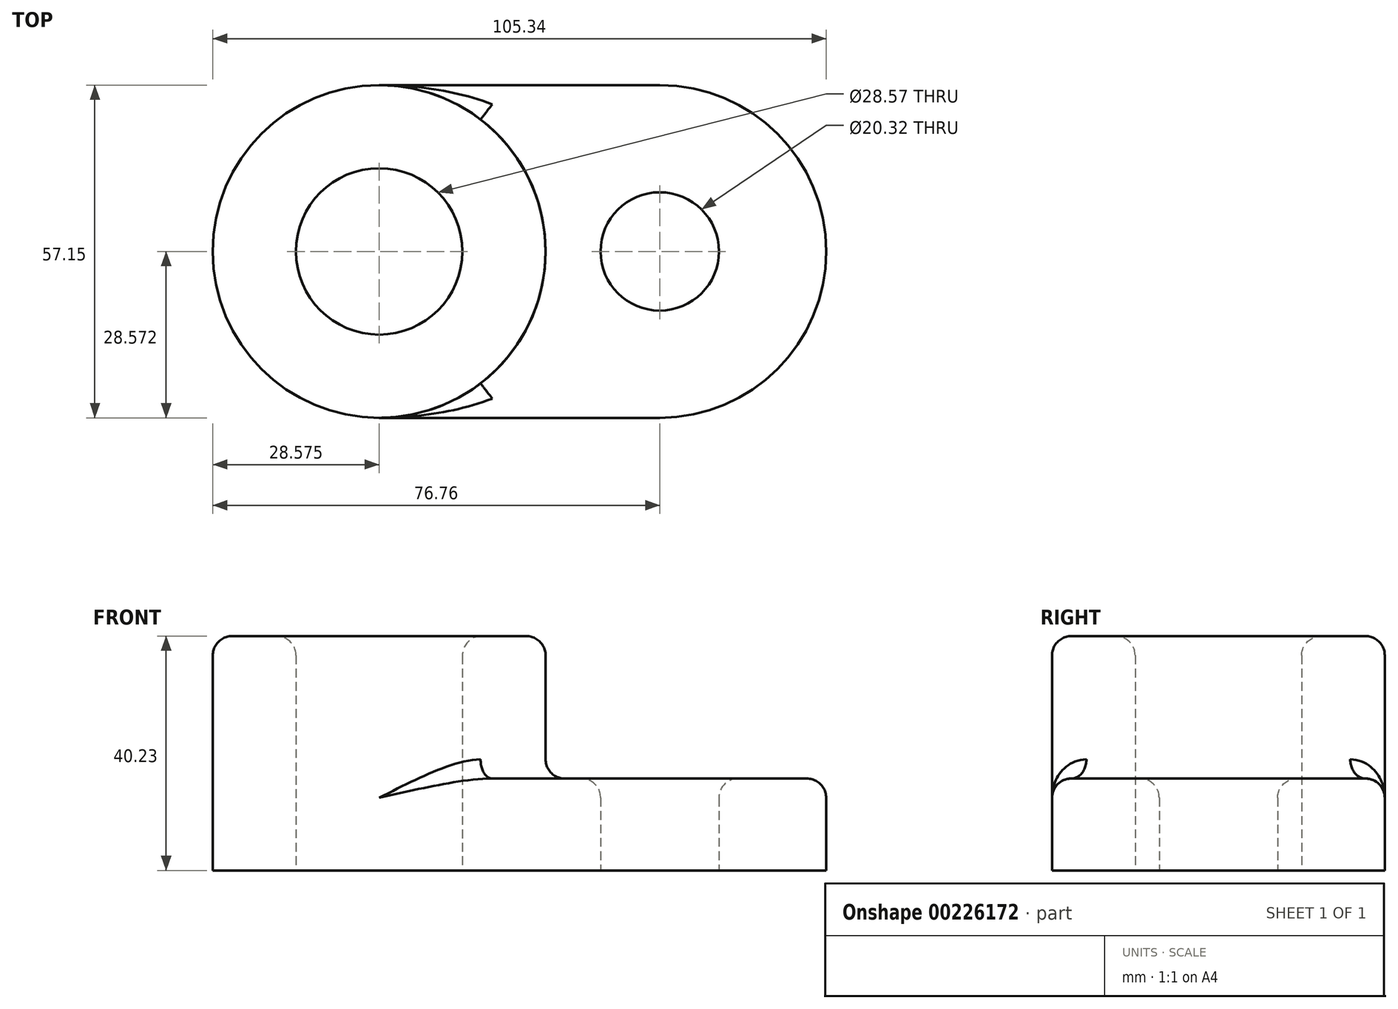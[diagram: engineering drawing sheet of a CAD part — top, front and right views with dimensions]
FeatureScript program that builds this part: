
annotation { "Feature Type Name" : "Feature", "Feature Type Description" : "" }
export const myFeature = defineFeature(function(context is Context, id is Id, definition is map)
    precondition{}
    {
        {
            var Q0;
            Q0=qCreatedBy(makeId("Top.planeOp"),FACE);
            var sketch = newSketch(context, id + "F0", { "sketchPlane" : qUnion([Q0])});
            skCircle(sketch, "E0", {"center": v(-32.27, 43.25) * mm, "radius": 28.58 * mm});
            skCircle(sketch, "E1", {"center": v(-32.27, 43.25) * mm, "radius": 14.29 * mm});
            skLineSegment(sketch, "E2", {"start": v(-32.27, 14.68) * mm, "end": v(-32.27, 71.83) * mm});
            skLineSegment(sketch, "E3", {"start": v(-32.27, 14.68) * mm, "end": v(15.91, 14.68) * mm});
            skLineSegment(sketch, "E4", {"start": v(-32.27, 71.83) * mm, "end": v(15.91, 71.83) * mm});
            skLineSegment(sketch, "E5", {"start": v(15.91, 14.68) * mm, "end": v(15.91, 71.83) * mm});
            skArc(sketch, "E6", {"start": v(15.91, 14.68) * mm, "mid": v(44.49, 43.25) * mm, "end": v(15.91, 71.83) * mm});
            skCircle(sketch, "E7", {"center": v(15.91, 43.25) * mm, "radius": 10.16 * mm});
            skPoint(sketch, "E8.right.end.orphan", {"position": v(-20.85, 28.66) * mm});
            skSolve(sketch);
        }
        {
            var Q0;
            {var subQ0=sQuery(id+"F0.wireOp",EDGE,"E2");var subQ4=sQuery(id+"F0.wireOp",EDGE,"E1");var subQ5=makeQuery(id+"F0.imprint","INTERSECT",VERTEX,{"disambiguationData":[OD(0.0)],"derivedFrom":[subQ4,subQ0]});Q0=makeQuery(id+"F0.imprint","IMPRINT",FACE,{"disambiguationData":[TD([[makeQuery(id+"F0.imprint","IMPRINT",EDGE,{"disambiguationData":[TD([[subQ5,1.0]])],"derivedFrom":subQ4}),-1.0]])]});}
            var Q1;
            {var subQ0=sQuery(id+"F0.wireOp",EDGE,"E2");var subQ4=sQuery(id+"F0.wireOp",EDGE,"E1");var subQ5=makeQuery(id+"F0.imprint","INTERSECT",VERTEX,{"disambiguationData":[OD(0.0)],"derivedFrom":[subQ4,subQ0]});Q1=makeQuery(id+"F0.imprint","IMPRINT",FACE,{"disambiguationData":[TD([[makeQuery(id+"F0.imprint","IMPRINT",EDGE,{"disambiguationData":[TD([[subQ5,-1.0]])],"derivedFrom":subQ4}),-1.0]])]});}
            extrude(context, id + "F1", {"entities" : qUnion([Q0, Q1]), "depth" : 40.23 * mm});
        }
        {
            var Q0;
            Q0=makeQuery(id+"F1.opExtrude","CAP_FACE",FACE,{"disambiguationData":[OSD([sQuery(id+"F0.wireOp",EDGE,"E0"),sQuery(id+"F0.wireOp",EDGE,"E1")])],"isStart":false});
            fillet(context, id + "F2", {"entities" : qUnion([Q0]), "radius" : 3.3 * mm, "tangentPropagation" : true, "allowEdgeOverflow" : false});
        }
        {
            var Q0;
            {var subQ2=sQuery(id+"F0.wireOp",EDGE,"E3");Q0=makeQuery(id+"F0.imprint","IMPRINT",FACE,{"disambiguationData":[TD([[makeQuery(id+"F0.imprint","IMPRINT",EDGE,{"derivedFrom":subQ2}),1.0]])]});}
            var Q1;
            {var subQ0=sQuery(id+"F0.wireOp",EDGE,"E6");Q1=makeQuery(id+"F0.imprint","IMPRINT",FACE,{"disambiguationData":[TD([[makeQuery(id+"F0.imprint","IMPRINT",EDGE,{"derivedFrom":subQ0}),1.0]])]});}
            extrude(context, id + "F3", {"entities" : qUnion([Q0, Q1]), "operationType" : NewBodyOperationType.ADD, "depth" : 15.77 * mm});
        }
        {
            var Q0;
            Q0=makeQuery(id+"F3.opExtrude","CAP_FACE",FACE,{"disambiguationData":[OSD([sQuery(id+"F0.wireOp",EDGE,"E0"),sQuery(id+"F0.wireOp",EDGE,"E3"),sQuery(id+"F0.wireOp",EDGE,"E4"),sQuery(id+"F0.wireOp",EDGE,"E6"),sQuery(id+"F0.wireOp",EDGE,"E7")])],"isStart":false});
            var Q1;
            Q1=makeQuery(id+"F3.opExtrude","CAP_EDGE",EDGE,{"disambiguationData":[OSD([sQuery(id+"F0.wireOp",EDGE,"E7")])],"isStart":false});
            fillet(context, id + "F4", {"entities" : qUnion([Q0, Q1]), "radius" : 3.3 * mm, "tangentPropagation" : true, "allowEdgeOverflow" : false});
        }
    });
